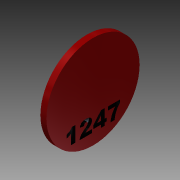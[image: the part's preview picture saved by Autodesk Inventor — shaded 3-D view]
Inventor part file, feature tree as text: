
AUTODESK INVENTOR PART (.ipt)
format: ipt  version: 2016 (Build 200138000, 138)  size: 647,680 bytes
history: native  units: in
note: dims shown in document units (in); Inventor stores cm internally (conversion verified against a paired STEP export)
features: sketch x23, extrude x17, plane x9, projected_geometry x5, loft x4, other x3, mirror x1, emboss x1, fillet x1
ambient origin geometry x8: Origin, YZ Plane, XZ Plane, XY Plane, X Axis, Y Axis, Z Axis, Center Point
bodies: Solid1 (feature_tree)
feature tree (64):
  sketch  "Sketch1"  dims[d0=0.7559in d1=0.7559in]
  plane  "Work Plane1"
  loft  "Loft1"
  extrude  "Extrusion1"  Depth=0.2in
  plane  "Work Plane4"
  loft  "Loft2"
  plane  "Work Plane5"
  loft  "Loft3"
  loft  "Loft4"
  extrude  "Extrusion2"  TaperAngle=0.0deg  [1 undecoded]
  plane  "Work Plane6"
  extrude  "Extrusion3"  Depth=1.0in
  extrude  "Extrusion4"  Depth=1.0651in
  extrude  "Extrusion5"  Depth=0.962in
  plane  "Work Plane7"
  extrude  "Extrusion6"  Depth=0.075in
  plane  "Work Plane8"
  other  "Work Axis1"
  plane  "Work Plane9"
  extrude  "Extrusion7"  Depth=0.06in
  mirror  "Mirror3"
  extrude  "Extrusion8"  Depth=0.05in
  plane  "Work Plane10"
  extrude  "Extrusion9"  Depth=0.0625in
  plane  "Work Plane11"
  extrude  "Extrusion10"  Depth=0.075in
  extrude  "Extrusion11"  TaperAngle=0.0deg  [1 undecoded]
  extrude  "Extrusion12"  Depth=0.2in
  extrude  "Extrusion13"  TaperAngle=0.0deg  [1 undecoded]
  emboss  "Emboss1"
  extrude  "Extrusion16"  Depth=0.01in
  extrude  "Extrusion17"  Depth=0.0344in
  extrude  "Extrusion18"  TaperAngle=60.0deg  [1 undecoded]
  fillet  "Fillet1"  [1 undecoded]
  extrude  "Extrusion20"  Depth=0.05in
  sketch  "Sketch2"  dims[d2=0.9963in d3=0.2in]
  sketch  "Sketch3"  dims[d4=0.5in d6=0.08in]
  sketch  "Sketch4"  dims[d7=0.55in d8=150.0deg]
  other  "Edges1"
  sketch  "Sketch5"  dims[d9=150.0deg d14=0.33in]
  projected_geometry  "Projected Loop1"
  other  "Edges2"
  sketch  "Sketch6"  dims[d15=0.66in d18=0.0in d19=90.0deg]
  sketch  "Sketch7"  dims[d20=0.0in d21=90.0deg d22=1.0in]
  sketch  "Sketch8"  dims[d26=1.0651in d28=1.0651in]
  sketch  "Sketch9"  dims[d29=0.0in d30=0.962in]
  sketch  "Sketch10"  dims[d31=0.962in d32=0.075in]
  sketch  "Sketch11"  dims[d33=0.15in d34=0.06in]
  sketch  "Sketch12"  dims[d35=0.1in d36=0.05in]
  sketch  "Sketch13"  dims[d37=0.45in d38=0.0in d39=0.0625in]
  projected_geometry  "Projected Loop2"
  projected_geometry  "Projected Loop3"
  sketch  "Sketch14"  dims[d40=0.01in d41=0.075in]
  projected_geometry  "Projected Loop4"
  sketch  "Sketch15"  dims[d42=0.01in d43=0.0in d44=90.0deg]
  sketch  "Sketch16"  dims[d45=0.0in d46=90.0deg d47=0.2in]
  sketch  "Sketch17"  dims[d48=0.07in d49=0.0in d50=90.0deg]
  sketch  "Sketch18"  dims[d51=0.0in d52=90.0deg d53=0.01in]
  sketch  "Sketch19"  dims[d54=0.01in d55=0.0344in]
  sketch  "Sketch23"  dims[d56=150.0deg d57=60.0deg d58=150.0deg]
  projected_geometry  "Projected Loop6"
  sketch  "Sketch24"  dims[d59=0.7in d60=0.05in]
  sketch  "Sketch25"  dims[d61=0.05in d62=0.05in]
  sketch  "Sketch27"  dims[d63=0.05in d64=0.05in d65=0.01in d66=0.0in d67=90.0deg d68=0.0in d69=90.0deg d70=0.1in d71=0.4in d72=0.15in d73=0.05in d74=0.0in d75=0.02in d77=0.15in d78=0.02in d79=0.1in d80=0.1in d81=0.1in d82=0.02in d83=0.15in d84=0.05in d85=0.0in d86=0.045in d87=0.0in d88=0.025in d89=0.0in d90=0.02in d91=0.02in d92=0.005in d93=0.0in d94=90.0deg d95=0.4466in d96=1.0in d97=0.0in d98=1.0in d99=0.0in d100=0.6528in d101=0.0in d102=0.0in d103=1.0in d104=0.0in d106=90.0deg d107=1.0in d108=0.0in d109=1.65in d110=0.1in d111=0.1in d112=0.0in d113=0.1in d114=0.075in d115=0.0in d116=0.05in d117=0.0in d123=0.84in d124=0.8in d125=0.0in d126=0.0in d127=1.0in d128=0.0in d130=0.15in d131=-0.0206in d135=0.2in d136=0.05in d137=0.1in d140=0.05in d141=0.1in d142=0.0in]
note: 5 required parameter values undecoded (feature->parameter linkage not recoverable at this tier; creation-order binding heuristic only, values carry confidence <= 0.55)
